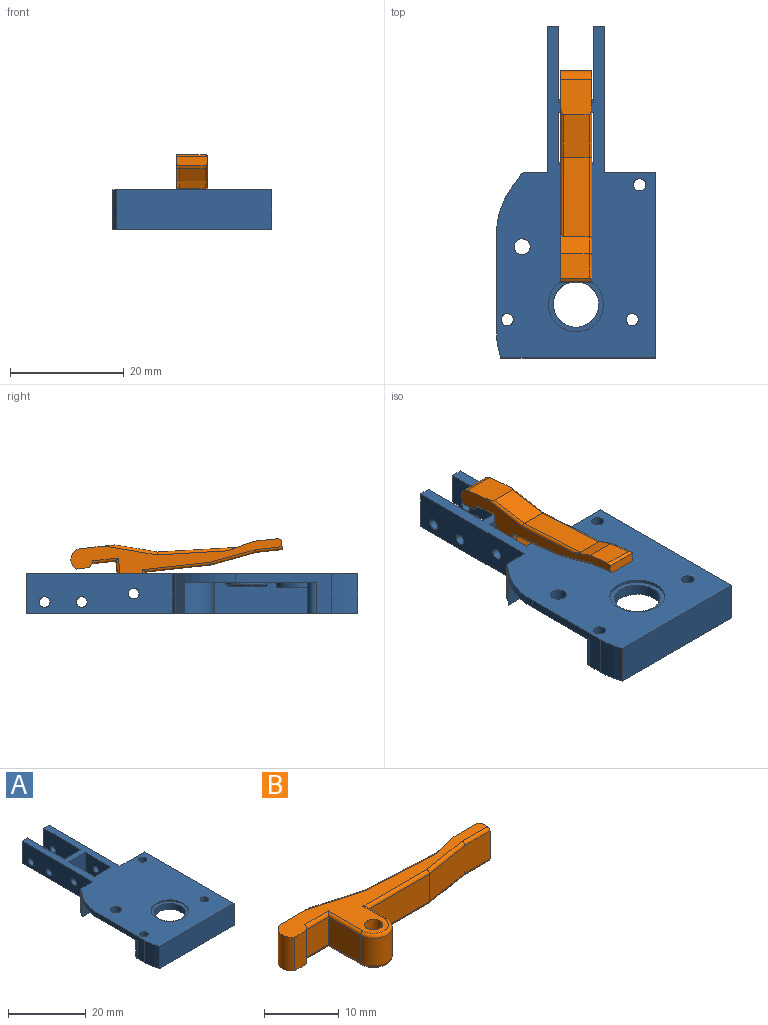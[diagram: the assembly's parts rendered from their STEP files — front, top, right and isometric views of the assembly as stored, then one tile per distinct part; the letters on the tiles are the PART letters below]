
ASSEMBLY  parts=2 mates=1
PART A: 68 faces, bbox 28x58.4x7 mm
  f0: plane 5.7x1.95mm, normal (0,1,0), area 11.1mm2, adj f1,f2,f36,f54
  f1: plane 25.8x7mm, normal (1,0,0), area 164.8mm2, adj f0,f3,f4,f18,f35,f36,f51,f52
  f2: plane 13.5x7mm, normal (-1,0,0), area 78.2mm2, adj f0,f3,f4,f19,f35,f36,f51,f52
  f3: plane 3.34x1.95mm, normal (0,0,-1), area 6.5mm2, adj f1,f2,f57,f61
  f4: plane 3.96x1.95mm, normal (0,0,-1), area 7.7mm2, adj f1,f2,f55,f58
  f5: plane 5.5x1.29mm, normal (1,0,0), area 7.1mm2, adj f35,f40,f42,f43
  f6: plane 5.5x0.8mm, normal (0,1,0), area 4.4mm2, adj f35,f40,f41,f43
  f7: plane 5.5x3.25mm, normal (0,1,0), area 17.8mm2, adj f8,f28,f35,f40
  f8: plane 5.5x4.2mm, normal (-1,0,0), area 23.1mm2, adj f7,f9,f35,f40
  f9: plane 5.5x3.25mm, normal (0,-1,0), area 17.8mm2, adj f8,f29,f35,f40
  f10: plane 7x6mm, normal (0,-1,0), area 42mm2, adj f11,f30,f35,f36
  f11: plane 9.3x7mm, normal (-1,0,0), area 58.9mm2, adj f10,f12,f35,f36,f53,f62
  f12: plane 6.5x6mm, normal (0,1,0), area 39mm2, adj f11,f30,f35,f62
  f13: cylinder r=11.2mm len=5.5mm, axis (0,0,1), area 14.1mm2, adj f33,f35,f40,f42
  f14: plane 17x7mm, normal (-1,0,0), area 40.4mm2, adj f15,f35,f36,f39,f40,f41
  f15: cylinder r=14mm len=7mm, axis (0,0,1), area 33mm2, adj f14,f16,f35,f36
  f16: plane 27.22x7mm, normal (0,-1,0), area 190.5mm2, adj f15,f17,f35,f36
  f17: plane 32.62x7mm, normal (1,0,0), area 228.4mm2, adj f16,f18,f35,f36
  f18: plane 9.05x7mm, normal (0,1,0), area 63.3mm2, adj f1,f17,f35,f36
  f19: plane 6.5x6mm, normal (0,1,0), area 39mm2, adj f2,f20,f35,f63
  f20: plane 13.5x7mm, normal (1,0,0), area 85.5mm2, adj f19,f21,f35,f36,f49,f50,f63
  f21: plane 7x1.95mm, normal (0,1,0), area 13.7mm2, adj f20,f22,f35,f36
  f22: plane 25.8x7mm, normal (-1,0,0), area 172.1mm2, adj f21,f23,f35,f36,f48,f49,f50
  f23: plane 7x3.99mm, normal (0,1,0), area 27.9mm2, adj f22,f35,f36,f47
  f24: plane 7x0.18mm, normal (-0.95,0.33,0), area 1.3mm2, adj f25,f35,f36,f47
  f25: plane 7x1.3mm, normal (-0.78,0.62,0), area 11.6mm2, adj f24,f26,f35,f36,f39
  f26: plane 17.02x5.5mm, normal (0,-1,0), area 93.6mm2, adj f25,f27,f35,f40
  f27: cylinder r=5.16mm len=5.5mm, axis (0,0,1), area 44.6mm2, adj f26,f28,f35,f40
  f28: plane 16.49x5.5mm, normal (-1,0,0), area 90.7mm2, adj f7,f27,f35,f40
  f29: cylinder r=11.2mm len=5.5mm, axis (0,0,1), area 14.1mm2, adj f9,f33,f35,f40
  f30: plane 9.3x7mm, normal (1,0,0), area 58.9mm2, adj f10,f12,f35,f36,f48,f62
  f31: cylinder r=1.07mm len=7mm, axis (0,0,1), area 47.3mm2, adj f35,f36
  f32: cylinder r=1.07mm len=7mm, axis (0,0,1), area 47.3mm2, adj f35,f36
  f33: plane 21.81x5.5mm, normal (0,1,0), area 120mm2, adj f13,f29,f35,f40
  f34: cylinder r=1.07mm len=7mm, axis (0,0,1), area 47.3mm2, adj f35,f36
  f35: plane 58.42x28mm, normal (0,0,-1), area 333.7mm2, adj f1,f2,f5,f6,f7,f8,f9,f10
  f36: plane 58.42x28mm, normal (0,0,1), area 923.3mm2, adj f0,f1,f2,f10,f11,f14,f15,f16
  f37: cylinder r=4mm len=8mm, axis (0,0,1), area 49mm2, adj f65,f67
  f38: cylinder r=1.4mm len=2.8mm, axis (0,0,1), area 20.2mm2, adj f36,f45
  f39: cylinder r=14mm len=8.85mm, axis (0,0,1), area 14.3mm2, adj f14,f25,f36,f40
  f40: plane 28.39x25.2mm, normal (0,0,-1), area 528.9mm2, adj f5,f6,f7,f8,f9,f13,f14,f26
  f41: cylinder r=1.5mm len=5.5mm, axis (0,0,1), area 13mm2, adj f6,f14,f35,f40
  f42: cylinder r=1.5mm len=5.5mm, axis (0,0,1), area 10.2mm2, adj f5,f13,f35,f40
  f43: cylinder r=1.5mm len=5.5mm, axis (0,0,1), area 13mm2, adj f5,f6,f35,f40
  f44: cylinder r=3.7mm len=7.4mm, axis (0,0,1), area 11.6mm2, adj f40,f46
  f45: plane 6.8x6.8mm, normal (0,0,-1), area 30.2mm2, adj f38,f46
  f46: cone r=3.7mm half-angle=45deg, axis (0,0,1), area 9.5mm2, adj f44,f45
  f47: cylinder r=1mm len=7mm, axis (0,0,1), area 8.7mm2, adj f23,f24,f35,f36
  f48: cylinder r=0.95mm len=1.95mm, axis (-1,0,0), area 11.6mm2, adj f22,f30
  f49: cylinder r=0.95mm len=1.95mm, axis (-1,0,0), area 11.6mm2, adj f20,f22
  f50: cylinder r=0.95mm len=1.95mm, axis (-1,0,0), area 11.6mm2, adj f20,f22
  f51: cylinder r=0.95mm len=1.95mm, axis (-1,0,0), area 11.6mm2, adj f1,f2
  f52: cylinder r=0.95mm len=1.95mm, axis (-1,0,0), area 11.6mm2, adj f1,f2
  f53: cylinder r=0.95mm len=1.95mm, axis (-1,0,0), area 11.6mm2, adj f1,f11
  f54: plane 1.95x1.5mm, normal (0,0,-1), area 2.9mm2, adj f0,f1,f2,f55
  f55: plane 1.95x1.3mm, normal (0,1,0), area 2.5mm2, adj f1,f2,f4,f54
  f56: plane 2.5x1.95mm, normal (0,0,-1), area 4.9mm2, adj f1,f2,f57,f58
  f57: plane 1.95x1.3mm, normal (0,1,0), area 2.5mm2, adj f1,f2,f3,f56
  f58: plane 1.95x1.3mm, normal (0,-1,0), area 2.5mm2, adj f1,f2,f4,f56
  f59: plane 1.95x1.6mm, normal (0,0,-1), area 3.1mm2, adj f1,f2,f60,f61
  f60: plane 1.95x1.3mm, normal (0,1,0), area 2.5mm2, adj f1,f2,f35,f59
  f61: plane 1.95x1.3mm, normal (0,-1,0), area 2.5mm2, adj f1,f2,f3,f59
  f62: plane 6x0.5mm, normal (0,0.71,0.71), area 4.2mm2, adj f11,f12,f30,f36
  f63: plane 6x0.5mm, normal (0,0.71,0.71), area 4.2mm2, adj f2,f19,f20,f36
  f64: cylinder r=5mm len=10mm, axis (0,0,1), area 29.8mm2, adj f40,f65
  f65: plane 10x10mm, normal (0,0,-1), area 28.3mm2, adj f37,f64
  f66: cylinder r=4.85mm len=9.7mm, axis (0,0,1), area 15.2mm2, adj f36,f67
  f67: plane 9.7x9.7mm, normal (0,0,1), area 23.6mm2, adj f37,f66
PART B: 40 faces, bbox 37.2x12.1x5.5 mm
  f0: plane 6.26x5.5mm, normal (0,1,0), area 34mm2, adj f1,f17,f18,f19,f30,f35
  f1: cylinder r=1.93mm len=5.5mm, axis (0,0,-1), area 25.3mm2, adj f0,f2,f18,f19
  f2: plane 5.5x2.26mm, normal (0,-1,0), area 12.4mm2, adj f1,f3,f18,f19
  f3: cylinder r=1.93mm len=5.5mm, axis (0,0,-1), area 4.7mm2, adj f2,f4,f18,f19,f20,f24
  f4: plane 4.5x4.24mm, normal (0,-1,0), area 19.1mm2, adj f3,f5,f20,f24
  f5: plane 6.01x4.5mm, normal (-1,0,0), area 27mm2, adj f4,f6,f21,f25
  f6: cylinder r=2.5mm len=5mm, axis (0,0,-1), area 35.3mm2, adj f5,f7,f22,f26
  f7: plane 4.5x3.5mm, normal (1,0,0), area 15.7mm2, adj f6,f8,f23,f27
  f8: plane 11.6x4.5mm, normal (0,-1,0), area 52.2mm2, adj f7,f9,f32,f37
  f9: plane 8.02x4.5mm, normal (0.16,-0.99,0), area 36.6mm2, adj f8,f10,f33,f38
  f10: plane 4.74x4.5mm, normal (0,-1,0), area 21.3mm2, adj f9,f11,f34,f39
  f11: plane 5.5x1.64mm, normal (1,0,0), area 8.9mm2, adj f10,f12,f18,f19,f28,f34,f39
  f12: plane 5.48x0.5mm, normal (0.58,0.81,0), area 3.3mm2, adj f11,f13,f18,f28
  f13: plane 5x4.32mm, normal (0,1,0), area 21.6mm2, adj f12,f14,f18,f28
  f14: plane 5x4.77mm, normal (-0.24,0.97,0), area 16mm2, adj f13,f15,f18,f29,f36
  f15: plane 14.03x4.5mm, normal (0.05,1,0), area 63.2mm2, adj f14,f17,f31,f36
  f16: cylinder r=1.2mm len=5.5mm, axis (0,0,-1), area 41.5mm2, adj f18,f19
  f17: plane 7.31x4.5mm, normal (0.27,0.96,0), area 34.2mm2, adj f0,f15,f30,f35
  f18: plane 37.19x10.87mm, normal (0,0,1), area 99mm2, adj f0,f1,f2,f3,f11,f12,f13,f14
  f19: plane 37.19x10.87mm, normal (0,0,-1), area 94.7mm2, adj f0,f1,f2,f3,f11,f16,f20,f21
  f20: cylinder r=0.5mm len=4.74mm, axis (1,0,0), area 3.4mm2, adj f3,f4,f19,f21
  f21: cylinder r=0.5mm len=6.51mm, axis (0,-1,0), area 4.9mm2, adj f5,f19,f20,f22
  f22: torus R=2mm, axis (0,0,1), area 5.7mm2, adj f6,f19,f21,f23
  f23: cylinder r=0.5mm len=4mm, axis (0,1,0), area 2.9mm2, adj f7,f19,f22,f32
  f24: cylinder r=0.5mm len=4.74mm, axis (-1,0,0), area 3.4mm2, adj f3,f4,f18,f25
  f25: cylinder r=0.5mm len=6.51mm, axis (0,1,0), area 4.9mm2, adj f5,f18,f24,f26
  f26: torus R=2mm, axis (0,0,1), area 5.7mm2, adj f6,f18,f25,f27
  f27: cylinder r=0.5mm len=4mm, axis (0,-1,0), area 2.9mm2, adj f7,f18,f26,f37
  f28: cylinder r=0.5mm len=4.82mm, axis (-1,0,0), area 3.6mm2, adj f11,f12,f13,f19,f29
  f29: cylinder r=0.5mm len=3.26mm, axis (-0.97,-0.24,0), area 2.5mm2, adj f14,f19,f28,f31
  f30: cylinder r=0.5mm len=9.2mm, axis (-0.96,0.27,0), area 6.5mm2, adj f0,f17,f19,f31
  f31: cylinder r=0.5mm len=14.18mm, axis (-1,0.05,0), area 11.1mm2, adj f15,f19,f29,f30
  f32: cylinder r=0.5mm len=12.1mm, axis (1,0,0), area 9.2mm2, adj f8,f19,f23,f33
  f33: cylinder r=0.5mm len=8.14mm, axis (0.99,0.16,0), area 6.4mm2, adj f9,f19,f32,f34
  f34: cylinder r=0.5mm len=4.78mm, axis (1,0,0), area 3.7mm2, adj f10,f11,f19,f33
  f35: cylinder r=0.5mm len=9.2mm, axis (0.96,-0.27,0), area 6.5mm2, adj f0,f17,f18,f36
  f36: cylinder r=0.5mm len=14.11mm, axis (1,-0.05,0), area 10.6mm2, adj f14,f15,f18,f35
  f37: cylinder r=0.5mm len=12.1mm, axis (-1,0,0), area 9.2mm2, adj f8,f18,f27,f38
  f38: cylinder r=0.5mm len=8.14mm, axis (-0.99,-0.16,0), area 6.4mm2, adj f9,f18,f37,f39
  f39: cylinder r=0.5mm len=4.78mm, axis (-1,0,0), area 3.7mm2, adj f10,f11,f18,f38
PLACE A at identity fixed
PLACE B rot(axis=(0.55,-0.62,-0.55),116.4deg) t=(2.8,34.85,-3.5)mm
MATE cylindrical A.f48 <-> B.f16  axis (-1,0,0) through (3,34.85,-3.5)mm
